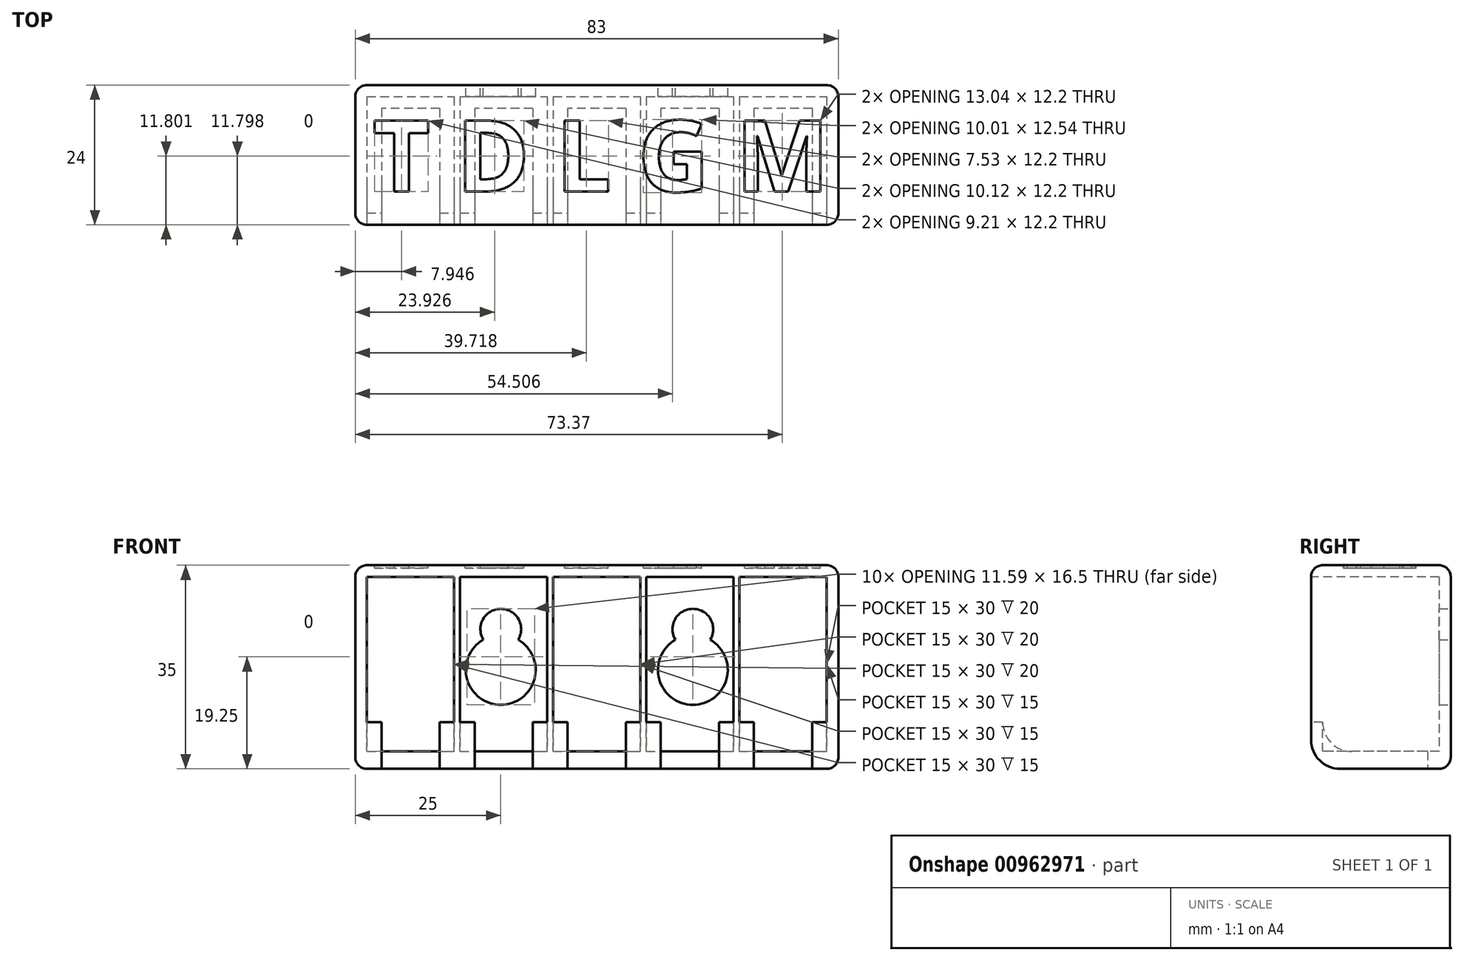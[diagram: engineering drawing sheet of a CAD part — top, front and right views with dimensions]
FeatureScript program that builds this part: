
annotation { "Feature Type Name" : "Feature", "Feature Type Description" : "" }
export const myFeature = defineFeature(function(context is Context, id is Id, definition is map)
    precondition{}
    {
        {
            var Q0;
            Q0=qCreatedBy(makeId("Top.planeOp"),FACE);
            var sketch = newSketch(context, id + "F0", { "sketchPlane" : qUnion([Q0])});
            skLineSegment(sketch, "E0.bottom", {"start": v(41.5, -12) * mm, "end": v(-41.5, -12) * mm});
            skLineSegment(sketch, "E0.top", {"start": v(41.5, 12) * mm, "end": v(-41.5, 12) * mm});
            skLineSegment(sketch, "E0.left", {"start": v(41.5, -12) * mm, "end": v(41.5, 12) * mm});
            skLineSegment(sketch, "E0.right", {"start": v(-41.5, -12) * mm, "end": v(-41.5, 12) * mm});
            skPoint(sketch, "E0.middle", {"position": v(0, 0) * mm});
            skSolve(sketch);
        }
        {
            var Q0;
            Q0 = qSketchRegion(id + "F0", true);
            extrude(context, id + "F1", {"entities" : qUnion([Q0]), "depth" : 35 * mm, "offsetDistance" : 25 * mm});
        }
        {
            var Q0;
            Q0=makeQuery(id+"F1.opExtrude","SWEPT_FACE",FACE,{"disambiguationData":[OSD([sQuery(id+"F0.wireOp",EDGE,"E0.bottom")])]});
            var sketch = newSketch(context, id + "F2", { "sketchPlane" : qUnion([Q0])});
            skLineSegment(sketch, "E1.bottom", {"start": v(-39.5, 33) * mm, "end": v(-24.5, 33) * mm});
            skLineSegment(sketch, "E1.top", {"start": v(-39.5, 8) * mm, "end": v(-24.5, 8) * mm});
            skLineSegment(sketch, "E1.left", {"start": v(-39.5, 33) * mm, "end": v(-39.5, 8) * mm});
            skLineSegment(sketch, "E1.right", {"start": v(-24.5, 33) * mm, "end": v(-24.5, 8) * mm});
            skLineSegment(sketch, "E2.bottom", {"start": v(-23.5, 33) * mm, "end": v(-8.5, 33) * mm});
            skLineSegment(sketch, "E2.top", {"start": v(-23.5, 8) * mm, "end": v(-8.5, 8) * mm});
            skLineSegment(sketch, "E2.left", {"start": v(-23.5, 33) * mm, "end": v(-23.5, 8) * mm});
            skLineSegment(sketch, "E2.right", {"start": v(-8.5, 33) * mm, "end": v(-8.5, 8) * mm});
            skLineSegment(sketch, "E3.bottom", {"start": v(-7.5, 33) * mm, "end": v(7.5, 33) * mm});
            skLineSegment(sketch, "E3.top", {"start": v(-7.5, 8) * mm, "end": v(7.5, 8) * mm});
            skLineSegment(sketch, "E3.left", {"start": v(-7.5, 33) * mm, "end": v(-7.5, 8) * mm});
            skLineSegment(sketch, "E3.right", {"start": v(7.5, 33) * mm, "end": v(7.5, 8) * mm});
            skLineSegment(sketch, "E4.bottom", {"start": v(8.5, 33) * mm, "end": v(23.5, 33) * mm});
            skLineSegment(sketch, "E4.top", {"start": v(8.5, 8) * mm, "end": v(23.5, 8) * mm});
            skLineSegment(sketch, "E4.left", {"start": v(8.5, 33) * mm, "end": v(8.5, 8) * mm});
            skLineSegment(sketch, "E4.right", {"start": v(23.5, 33) * mm, "end": v(23.5, 8) * mm});
            skLineSegment(sketch, "E5.bottom", {"start": v(24.5, 33) * mm, "end": v(39.5, 33) * mm});
            skLineSegment(sketch, "E5.top", {"start": v(24.5, 8) * mm, "end": v(39.5, 8) * mm});
            skLineSegment(sketch, "E5.left", {"start": v(24.5, 33) * mm, "end": v(24.5, 8) * mm});
            skLineSegment(sketch, "E5.right", {"start": v(39.5, 33) * mm, "end": v(39.5, 8) * mm});
            skSolve(sketch);
        }
        {
            var Q0;
            Q0 = qSketchRegion(id + "F2", true);
            extrude(context, id + "F3", {"entities" : qUnion([Q0]), "operationType" : NewBodyOperationType.REMOVE, "oppositeDirection" : true, "depth" : 22 * mm, "offsetDistance" : 25 * mm});
        }
        {
            var Q0;
            Q0=makeQuery(id+"F3.boolean.opBoolean","COPY",FACE,{"derivedFrom":makeQuery(id+"F3.opExtrude","SWEPT_FACE",FACE,{"disambiguationData":[OSD([sQuery(id+"F2.wireOp",EDGE,"E1.top")])]})});
            var sketch = newSketch(context, id + "F4", { "sketchPlane" : qUnion([Q0])});
            skLineSegment(sketch, "E6.bottom", {"start": v(-39.5, 10) * mm, "end": v(-24.5, 10) * mm});
            skLineSegment(sketch, "E6.top", {"start": v(-39.5, -10) * mm, "end": v(-24.5, -10) * mm});
            skLineSegment(sketch, "E6.left", {"start": v(-39.5, 10) * mm, "end": v(-39.5, -10) * mm});
            skLineSegment(sketch, "E6.right", {"start": v(-24.5, 10) * mm, "end": v(-24.5, -10) * mm});
            skSolve(sketch);
        }
        {
            var Q0;
            Q0 = qSketchRegion(id + "F4", true);
            extrude(context, id + "F5", {"entities" : qUnion([Q0]), "operationType" : NewBodyOperationType.REMOVE, "oppositeDirection" : true, "depth" : 5 * mm, "offsetDistance" : 25 * mm});
        }
        {
            var Q0;
            Q0=makeQuery(id+"F3.boolean.opBoolean","COPY",FACE,{"derivedFrom":makeQuery(id+"F3.opExtrude","SWEPT_FACE",FACE,{"disambiguationData":[OSD([sQuery(id+"F2.wireOp",EDGE,"E2.top")])]})});
            var sketch = newSketch(context, id + "F6", { "sketchPlane" : qUnion([Q0])});
            skLineSegment(sketch, "E7.bottom", {"start": v(-23.5, 10) * mm, "end": v(-8.5, 10) * mm});
            skLineSegment(sketch, "E7.top", {"start": v(-23.5, -10) * mm, "end": v(-8.5, -10) * mm});
            skLineSegment(sketch, "E7.left", {"start": v(-23.5, 10) * mm, "end": v(-23.5, -10) * mm});
            skLineSegment(sketch, "E7.right", {"start": v(-8.5, 10) * mm, "end": v(-8.5, -10) * mm});
            skSolve(sketch);
        }
        {
            var Q0;
            Q0=makeQuery(id+"F6.imprint","IMPRINT",FACE,{"disambiguationData":[TD([[makeQuery(id+"F6.imprint","IMPRINT",EDGE,{"derivedFrom":sQuery(id+"F6.wireOp",EDGE,"E7.bottom")}),-1.0]])]});
            extrude(context, id + "F7", {"entities" : qUnion([Q0]), "operationType" : NewBodyOperationType.REMOVE, "oppositeDirection" : true, "depth" : 5 * mm, "offsetDistance" : 25 * mm});
        }
        {
            var Q0;
            Q0=makeQuery(id+"F3.boolean.opBoolean","COPY",FACE,{"derivedFrom":makeQuery(id+"F3.opExtrude","SWEPT_FACE",FACE,{"disambiguationData":[OSD([sQuery(id+"F2.wireOp",EDGE,"E3.top")])]})});
            var sketch = newSketch(context, id + "F8", { "sketchPlane" : qUnion([Q0])});
            skLineSegment(sketch, "E8.bottom", {"start": v(-7.5, 10) * mm, "end": v(7.5, 10) * mm});
            skLineSegment(sketch, "E8.top", {"start": v(-7.5, -10) * mm, "end": v(7.5, -10) * mm});
            skLineSegment(sketch, "E8.left", {"start": v(-7.5, 10) * mm, "end": v(-7.5, -10) * mm});
            skLineSegment(sketch, "E8.right", {"start": v(7.5, 10) * mm, "end": v(7.5, -10) * mm});
            skSolve(sketch);
        }
        {
            var Q0;
            Q0 = qSketchRegion(id + "F8", true);
            extrude(context, id + "F9", {"entities" : qUnion([Q0]), "operationType" : NewBodyOperationType.REMOVE, "oppositeDirection" : true, "depth" : 5 * mm, "offsetDistance" : 25 * mm});
        }
        {
            var Q0;
            Q0=makeQuery(id+"F3.boolean.opBoolean","COPY",FACE,{"derivedFrom":makeQuery(id+"F3.opExtrude","SWEPT_FACE",FACE,{"disambiguationData":[OSD([sQuery(id+"F2.wireOp",EDGE,"E4.top")])]})});
            var sketch = newSketch(context, id + "F10", { "sketchPlane" : qUnion([Q0])});
            skLineSegment(sketch, "E9.bottom", {"start": v(8.5, 10) * mm, "end": v(23.5, 10) * mm});
            skLineSegment(sketch, "E9.top", {"start": v(8.5, -10) * mm, "end": v(23.5, -10) * mm});
            skLineSegment(sketch, "E9.left", {"start": v(8.5, 10) * mm, "end": v(8.5, -10) * mm});
            skLineSegment(sketch, "E9.right", {"start": v(23.5, 10) * mm, "end": v(23.5, -10) * mm});
            skSolve(sketch);
        }
        {
            var Q0;
            Q0 = qSketchRegion(id + "F10", true);
            extrude(context, id + "F11", {"entities" : qUnion([Q0]), "operationType" : NewBodyOperationType.REMOVE, "oppositeDirection" : true, "depth" : 5 * mm, "offsetDistance" : 25 * mm});
        }
        {
            var Q0;
            Q0=makeQuery(id+"F3.boolean.opBoolean","COPY",FACE,{"derivedFrom":makeQuery(id+"F3.opExtrude","SWEPT_FACE",FACE,{"disambiguationData":[OSD([sQuery(id+"F2.wireOp",EDGE,"E5.top")])]})});
            var sketch = newSketch(context, id + "F12", { "sketchPlane" : qUnion([Q0])});
            skLineSegment(sketch, "E10.bottom", {"start": v(24.5, 10) * mm, "end": v(39.5, 10) * mm});
            skLineSegment(sketch, "E10.top", {"start": v(24.5, -10) * mm, "end": v(39.5, -10) * mm});
            skLineSegment(sketch, "E10.left", {"start": v(24.5, 10) * mm, "end": v(24.5, -10) * mm});
            skLineSegment(sketch, "E10.right", {"start": v(39.5, 10) * mm, "end": v(39.5, -10) * mm});
            skSolve(sketch);
        }
        {
            var Q0;
            Q0 = qSketchRegion(id + "F12", true);
            extrude(context, id + "F13", {"entities" : qUnion([Q0]), "operationType" : NewBodyOperationType.REMOVE, "oppositeDirection" : true, "depth" : 5 * mm, "offsetDistance" : 25 * mm});
        }
        {
            var Q0;
            Q0=makeQuery(id+"F1.opExtrude","SWEPT_FACE",FACE,{"disambiguationData":[OSD([sQuery(id+"F0.wireOp",EDGE,"E0.top")])]});
            var sketch = newSketch(context, id + "F14", { "sketchPlane" : qUnion([Q0])});
            skCircle(sketch, "E11", {"center": v(-16.5, 24) * mm, "radius": 3.5 * mm});
            skCircle(sketch, "E12", {"center": v(16.5, 24) * mm, "radius": 3.5 * mm});
            skCircle(sketch, "E13", {"center": v(-16.5, 17) * mm, "radius": 6 * mm});
            skCircle(sketch, "E14", {"center": v(16.5, 17) * mm, "radius": 6 * mm});
            skSolve(sketch);
        }
        {
            var Q0;
            Q0 = qSketchRegion(id + "F14", true);
            extrude(context, id + "F15", {"entities" : qUnion([Q0]), "operationType" : NewBodyOperationType.REMOVE, "endBound" : BoundingType.UP_TO_NEXT, "oppositeDirection" : true, "depth" : 25 * mm, "offsetDistance" : 25 * mm});
        }
        {
            var Q0;
            Q0=makeQuery(id+"F1.opExtrude","SWEPT_FACE",FACE,{"disambiguationData":[OSD([sQuery(id+"F0.wireOp",EDGE,"E0.bottom")])]});
            var sketch = newSketch(context, id + "F16", { "sketchPlane" : qUnion([Q0])});
            skLineSegment(sketch, "E15.bottom", {"start": v(-37, 8) * mm, "end": v(-27, 8) * mm});
            skLineSegment(sketch, "E15.top", {"start": v(-37, 0) * mm, "end": v(-27, 0) * mm});
            skLineSegment(sketch, "E15.left", {"start": v(-37, 8) * mm, "end": v(-37, 0) * mm});
            skLineSegment(sketch, "E15.right", {"start": v(-27, 8) * mm, "end": v(-27, 0) * mm});
            skLineSegment(sketch, "E16.bottom", {"start": v(-21, 8) * mm, "end": v(-11, 8) * mm});
            skLineSegment(sketch, "E16.top", {"start": v(-21, 0) * mm, "end": v(-11, 0) * mm});
            skLineSegment(sketch, "E16.left", {"start": v(-21, 8) * mm, "end": v(-21, 0) * mm});
            skLineSegment(sketch, "E16.right", {"start": v(-11, 8) * mm, "end": v(-11, 0) * mm});
            skLineSegment(sketch, "E17.bottom", {"start": v(-5, 8) * mm, "end": v(5, 8) * mm});
            skLineSegment(sketch, "E17.top", {"start": v(-5, 0) * mm, "end": v(5, 0) * mm});
            skLineSegment(sketch, "E17.left", {"start": v(-5, 8) * mm, "end": v(-5, 0) * mm});
            skLineSegment(sketch, "E17.right", {"start": v(5, 8) * mm, "end": v(5, 0) * mm});
            skLineSegment(sketch, "E18.bottom", {"start": v(11, 8) * mm, "end": v(21, 8) * mm});
            skLineSegment(sketch, "E18.top", {"start": v(11, 0) * mm, "end": v(21, 0) * mm});
            skLineSegment(sketch, "E18.left", {"start": v(11, 8) * mm, "end": v(11, 0) * mm});
            skLineSegment(sketch, "E18.right", {"start": v(21, 8) * mm, "end": v(21, 0) * mm});
            skLineSegment(sketch, "E19.bottom", {"start": v(27, 8) * mm, "end": v(37, 8) * mm});
            skLineSegment(sketch, "E19.top", {"start": v(27, 0) * mm, "end": v(37, 0) * mm});
            skLineSegment(sketch, "E19.left", {"start": v(27, 8) * mm, "end": v(27, 0) * mm});
            skLineSegment(sketch, "E19.right", {"start": v(37, 8) * mm, "end": v(37, 0) * mm});
            skSolve(sketch);
        }
        {
            var Q0;
            Q0 = qSketchRegion(id + "F16", true);
            extrude(context, id + "F17", {"entities" : qUnion([Q0]), "operationType" : NewBodyOperationType.REMOVE, "oppositeDirection" : true, "depth" : 20 * mm, "offsetDistance" : 25 * mm});
        }
        {
            var Q0;
            {var subQ0=sQuery(id+"F12.wireOp",EDGE,"E10.top");Q0=makeQuery(id+"F17.boolean.opBoolean","SPLIT",EDGE,{"disambiguationData":[TD([makeQuery(id+"F3.boolean.opBoolean","COPY",FACE,{"derivedFrom":makeQuery(id+"F3.opExtrude","SWEPT_FACE",FACE,{"disambiguationData":[OSD([sQuery(id+"F2.wireOp",EDGE,"E5.right")])]})})])],"derivedFrom":makeQuery(id+"F13.boolean.opBoolean","COPY",EDGE,{"derivedFrom":makeQuery(id+"F13.opExtrude","CAP_EDGE",EDGE,{"disambiguationData":[OSD([subQ0])],"isStart":false})})});}
            var Q1;
            {var subQ0=sQuery(id+"F12.wireOp",EDGE,"E10.top");Q1=makeQuery(id+"F17.boolean.opBoolean","SPLIT",EDGE,{"disambiguationData":[TD([makeQuery(id+"F3.boolean.opBoolean","COPY",FACE,{"derivedFrom":makeQuery(id+"F3.opExtrude","SWEPT_FACE",FACE,{"disambiguationData":[OSD([sQuery(id+"F2.wireOp",EDGE,"E5.left")])]})})])],"derivedFrom":makeQuery(id+"F13.boolean.opBoolean","COPY",EDGE,{"derivedFrom":makeQuery(id+"F13.opExtrude","CAP_EDGE",EDGE,{"disambiguationData":[OSD([subQ0])],"isStart":false})})});}
            var Q2;
            {var subQ0=sQuery(id+"F10.wireOp",EDGE,"E9.top");Q2=makeQuery(id+"F17.boolean.opBoolean","SPLIT",EDGE,{"disambiguationData":[TD([makeQuery(id+"F3.boolean.opBoolean","COPY",FACE,{"derivedFrom":makeQuery(id+"F3.opExtrude","SWEPT_FACE",FACE,{"disambiguationData":[OSD([sQuery(id+"F2.wireOp",EDGE,"E4.right")])]})})])],"derivedFrom":makeQuery(id+"F11.boolean.opBoolean","COPY",EDGE,{"derivedFrom":makeQuery(id+"F11.opExtrude","CAP_EDGE",EDGE,{"disambiguationData":[OSD([subQ0])],"isStart":false})})});}
            var Q3;
            {var subQ0=sQuery(id+"F10.wireOp",EDGE,"E9.top");Q3=makeQuery(id+"F17.boolean.opBoolean","SPLIT",EDGE,{"disambiguationData":[TD([makeQuery(id+"F3.boolean.opBoolean","COPY",FACE,{"derivedFrom":makeQuery(id+"F3.opExtrude","SWEPT_FACE",FACE,{"disambiguationData":[OSD([sQuery(id+"F2.wireOp",EDGE,"E4.left")])]})})])],"derivedFrom":makeQuery(id+"F11.boolean.opBoolean","COPY",EDGE,{"derivedFrom":makeQuery(id+"F11.opExtrude","CAP_EDGE",EDGE,{"disambiguationData":[OSD([subQ0])],"isStart":false})})});}
            var Q4;
            {var subQ0=sQuery(id+"F8.wireOp",EDGE,"E8.top");Q4=makeQuery(id+"F17.boolean.opBoolean","SPLIT",EDGE,{"disambiguationData":[TD([makeQuery(id+"F3.boolean.opBoolean","COPY",FACE,{"derivedFrom":makeQuery(id+"F3.opExtrude","SWEPT_FACE",FACE,{"disambiguationData":[OSD([sQuery(id+"F2.wireOp",EDGE,"E3.right")])]})})])],"derivedFrom":makeQuery(id+"F9.boolean.opBoolean","COPY",EDGE,{"derivedFrom":makeQuery(id+"F9.opExtrude","CAP_EDGE",EDGE,{"disambiguationData":[OSD([subQ0])],"isStart":false})})});}
            var Q5;
            {var subQ0=sQuery(id+"F8.wireOp",EDGE,"E8.top");Q5=makeQuery(id+"F17.boolean.opBoolean","SPLIT",EDGE,{"disambiguationData":[TD([makeQuery(id+"F3.boolean.opBoolean","COPY",FACE,{"derivedFrom":makeQuery(id+"F3.opExtrude","SWEPT_FACE",FACE,{"disambiguationData":[OSD([sQuery(id+"F2.wireOp",EDGE,"E3.left")])]})})])],"derivedFrom":makeQuery(id+"F9.boolean.opBoolean","COPY",EDGE,{"derivedFrom":makeQuery(id+"F9.opExtrude","CAP_EDGE",EDGE,{"disambiguationData":[OSD([subQ0])],"isStart":false})})});}
            var Q6;
            {var subQ0=sQuery(id+"F6.wireOp",EDGE,"E7.top");Q6=makeQuery(id+"F17.boolean.opBoolean","SPLIT",EDGE,{"disambiguationData":[TD([makeQuery(id+"F3.boolean.opBoolean","COPY",FACE,{"derivedFrom":makeQuery(id+"F3.opExtrude","SWEPT_FACE",FACE,{"disambiguationData":[OSD([sQuery(id+"F2.wireOp",EDGE,"E2.right")])]})})])],"derivedFrom":makeQuery(id+"F7.boolean.opBoolean","COPY",EDGE,{"derivedFrom":makeQuery(id+"F7.opExtrude","CAP_EDGE",EDGE,{"disambiguationData":[OSD([subQ0])],"isStart":false})})});}
            var Q7;
            {var subQ0=sQuery(id+"F6.wireOp",EDGE,"E7.top");Q7=makeQuery(id+"F17.boolean.opBoolean","SPLIT",EDGE,{"disambiguationData":[TD([makeQuery(id+"F3.boolean.opBoolean","COPY",FACE,{"derivedFrom":makeQuery(id+"F3.opExtrude","SWEPT_FACE",FACE,{"disambiguationData":[OSD([sQuery(id+"F2.wireOp",EDGE,"E2.left")])]})})])],"derivedFrom":makeQuery(id+"F7.boolean.opBoolean","COPY",EDGE,{"derivedFrom":makeQuery(id+"F7.opExtrude","CAP_EDGE",EDGE,{"disambiguationData":[OSD([subQ0])],"isStart":false})})});}
            var Q8;
            {var subQ0=sQuery(id+"F4.wireOp",EDGE,"E6.top");Q8=makeQuery(id+"F17.boolean.opBoolean","SPLIT",EDGE,{"disambiguationData":[TD([makeQuery(id+"F3.boolean.opBoolean","COPY",FACE,{"derivedFrom":makeQuery(id+"F3.opExtrude","SWEPT_FACE",FACE,{"disambiguationData":[OSD([sQuery(id+"F2.wireOp",EDGE,"E1.right")])]})})])],"derivedFrom":makeQuery(id+"F5.boolean.opBoolean","COPY",EDGE,{"derivedFrom":makeQuery(id+"F5.opExtrude","CAP_EDGE",EDGE,{"disambiguationData":[OSD([subQ0])],"isStart":false})})});}
            var Q9;
            {var subQ0=sQuery(id+"F4.wireOp",EDGE,"E6.top");Q9=makeQuery(id+"F17.boolean.opBoolean","SPLIT",EDGE,{"disambiguationData":[TD([makeQuery(id+"F3.boolean.opBoolean","COPY",FACE,{"derivedFrom":makeQuery(id+"F3.opExtrude","SWEPT_FACE",FACE,{"disambiguationData":[OSD([sQuery(id+"F2.wireOp",EDGE,"E1.left")])]})})])],"derivedFrom":makeQuery(id+"F5.boolean.opBoolean","COPY",EDGE,{"derivedFrom":makeQuery(id+"F5.opExtrude","CAP_EDGE",EDGE,{"disambiguationData":[OSD([subQ0])],"isStart":false})})});}
            var Q10;
            {var subQ0=sQuery(id+"F0.wireOp",EDGE,"E0.bottom");var subQ1=sQuery(id+"F0.wireOp",EDGE,"E0.right");Q10=makeQuery(id+"F17.boolean.opBoolean","SPLIT",EDGE,{"disambiguationData":[TD([makeQuery(id+"F1.opExtrude","SWEPT_FACE",FACE,{"disambiguationData":[OSD([subQ1])]})])],"derivedFrom":makeQuery(id+"F1.opExtrude","CAP_EDGE",EDGE,{"disambiguationData":[OSD([subQ0])],"isStart":true})});}
            var Q11;
            {var subQ0=sQuery(id+"F0.wireOp",EDGE,"E0.bottom");Q11=makeQuery(id+"F17.boolean.opBoolean","SPLIT",EDGE,{"disambiguationData":[TD([makeQuery(id+"F17.opExtrude","SWEPT_FACE",FACE,{"disambiguationData":[OSD([sQuery(id+"F16.wireOp",EDGE,"E15.right")])]})])],"derivedFrom":makeQuery(id+"F1.opExtrude","CAP_EDGE",EDGE,{"disambiguationData":[OSD([subQ0])],"isStart":true})});}
            var Q12;
            {var subQ0=sQuery(id+"F0.wireOp",EDGE,"E0.bottom");Q12=makeQuery(id+"F17.boolean.opBoolean","SPLIT",EDGE,{"disambiguationData":[TD([makeQuery(id+"F17.opExtrude","SWEPT_FACE",FACE,{"disambiguationData":[OSD([sQuery(id+"F16.wireOp",EDGE,"E16.right")])]})])],"derivedFrom":makeQuery(id+"F1.opExtrude","CAP_EDGE",EDGE,{"disambiguationData":[OSD([subQ0])],"isStart":true})});}
            var Q13;
            {var subQ0=sQuery(id+"F0.wireOp",EDGE,"E0.bottom");Q13=makeQuery(id+"F17.boolean.opBoolean","SPLIT",EDGE,{"disambiguationData":[TD([makeQuery(id+"F17.opExtrude","SWEPT_FACE",FACE,{"disambiguationData":[OSD([sQuery(id+"F16.wireOp",EDGE,"E17.right")])]})])],"derivedFrom":makeQuery(id+"F1.opExtrude","CAP_EDGE",EDGE,{"disambiguationData":[OSD([subQ0])],"isStart":true})});}
            var Q14;
            {var subQ0=sQuery(id+"F0.wireOp",EDGE,"E0.bottom");Q14=makeQuery(id+"F17.boolean.opBoolean","SPLIT",EDGE,{"disambiguationData":[TD([makeQuery(id+"F17.opExtrude","SWEPT_FACE",FACE,{"disambiguationData":[OSD([sQuery(id+"F16.wireOp",EDGE,"E18.right")])]})])],"derivedFrom":makeQuery(id+"F1.opExtrude","CAP_EDGE",EDGE,{"disambiguationData":[OSD([subQ0])],"isStart":true})});}
            var Q15;
            {var subQ0=sQuery(id+"F0.wireOp",EDGE,"E0.bottom");var subQ1=sQuery(id+"F0.wireOp",EDGE,"E0.left");Q15=makeQuery(id+"F17.boolean.opBoolean","SPLIT",EDGE,{"disambiguationData":[TD([makeQuery(id+"F1.opExtrude","SWEPT_FACE",FACE,{"disambiguationData":[OSD([subQ1])]})])],"derivedFrom":makeQuery(id+"F1.opExtrude","CAP_EDGE",EDGE,{"disambiguationData":[OSD([subQ0])],"isStart":true})});}
            fillet(context, id + "F18", {"entities" : qUnion([Q0, Q1, Q2, Q3, Q4, Q5, Q6, Q7, Q8, Q9, Q10, Q11, Q12, Q13, Q14, Q15]), "radius" : 5 * mm, "tangentPropagation" : true, "allowEdgeOverflow" : false});
        }
        {
            var Q0;
            Q0=makeQuery(id+"F1.opExtrude","CAP_FACE",FACE,{"disambiguationData":[OSD([sQuery(id+"F0.wireOp",EDGE,"E0.bottom"),sQuery(id+"F0.wireOp",EDGE,"E0.top"),sQuery(id+"F0.wireOp",EDGE,"E0.left"),sQuery(id+"F0.wireOp",EDGE,"E0.right")])],"isStart":false});
            var sketch = newSketch(context, id + "F19", { "sketchPlane" : qUnion([Q0])});
            skText(sketch, "E20", { "text": "T D L G M", "fontName": "OpenSans-Bold.ttf"});
            const initialGuessF19  = {"E20": [-0.0385, -0.0063, 1, 0, 0.0123]};
            skSetInitialGuess(sketch, initialGuessF19);
            skSolve(sketch);
        }
        {
            var Q0;
            Q0 = qSketchRegion(id + "F19", true);
            extrude(context, id + "F20", {"entities" : qUnion([Q0]), "operationType" : NewBodyOperationType.REMOVE, "oppositeDirection" : true, "depth" : 0.5 * mm, "offsetDistance" : 25 * mm});
        }
        {
            var Q0;
            Q0=makeQuery(id+"F1.opExtrude","CAP_EDGE",EDGE,{"disambiguationData":[OSD([sQuery(id+"F0.wireOp",EDGE,"E0.right")])],"isStart":false});
            var Q1;
            Q1=makeQuery(id+"F1.opExtrude","CAP_EDGE",EDGE,{"disambiguationData":[OSD([sQuery(id+"F0.wireOp",EDGE,"E0.bottom")])],"isStart":false});
            var Q2;
            Q2=makeQuery(id+"F1.opExtrude","CAP_EDGE",EDGE,{"disambiguationData":[OSD([sQuery(id+"F0.wireOp",EDGE,"E0.left")])],"isStart":false});
            var Q3;
            Q3=makeQuery(id+"F1.opExtrude","SWEPT_EDGE",EDGE,{"disambiguationData":[OSD([sQuery(id+"F0.wireOp",EDGE,"E0.bottom"),sQuery(id+"F0.wireOp",EDGE,"E0.right")])]});
            var Q4;
            Q4=makeQuery(id+"F1.opExtrude","SWEPT_EDGE",EDGE,{"disambiguationData":[OSD([sQuery(id+"F0.wireOp",EDGE,"E0.bottom"),sQuery(id+"F0.wireOp",EDGE,"E0.left")])]});
            var Q5;
            Q5=makeQuery(id+"F1.opExtrude","CAP_EDGE",EDGE,{"disambiguationData":[OSD([sQuery(id+"F0.wireOp",EDGE,"E0.top")])],"isStart":false});
            var Q6;
            Q6=makeQuery(id+"F1.opExtrude","SWEPT_EDGE",EDGE,{"disambiguationData":[OSD([sQuery(id+"F0.wireOp",EDGE,"E0.top"),sQuery(id+"F0.wireOp",EDGE,"E0.right")])]});
            var Q7;
            Q7=makeQuery(id+"F1.opExtrude","CAP_EDGE",EDGE,{"disambiguationData":[OSD([sQuery(id+"F0.wireOp",EDGE,"E0.top")])],"isStart":true});
            var Q8;
            Q8=makeQuery(id+"F1.opExtrude","SWEPT_EDGE",EDGE,{"disambiguationData":[OSD([sQuery(id+"F0.wireOp",EDGE,"E0.top"),sQuery(id+"F0.wireOp",EDGE,"E0.left")])]});
            fillet(context, id + "F21", {"entities" : qUnion([Q0, Q1, Q2, Q3, Q4, Q5, Q6, Q7, Q8]), "radius" : 2 * mm, "tangentPropagation" : true, "allowEdgeOverflow" : false});
        }
    });
